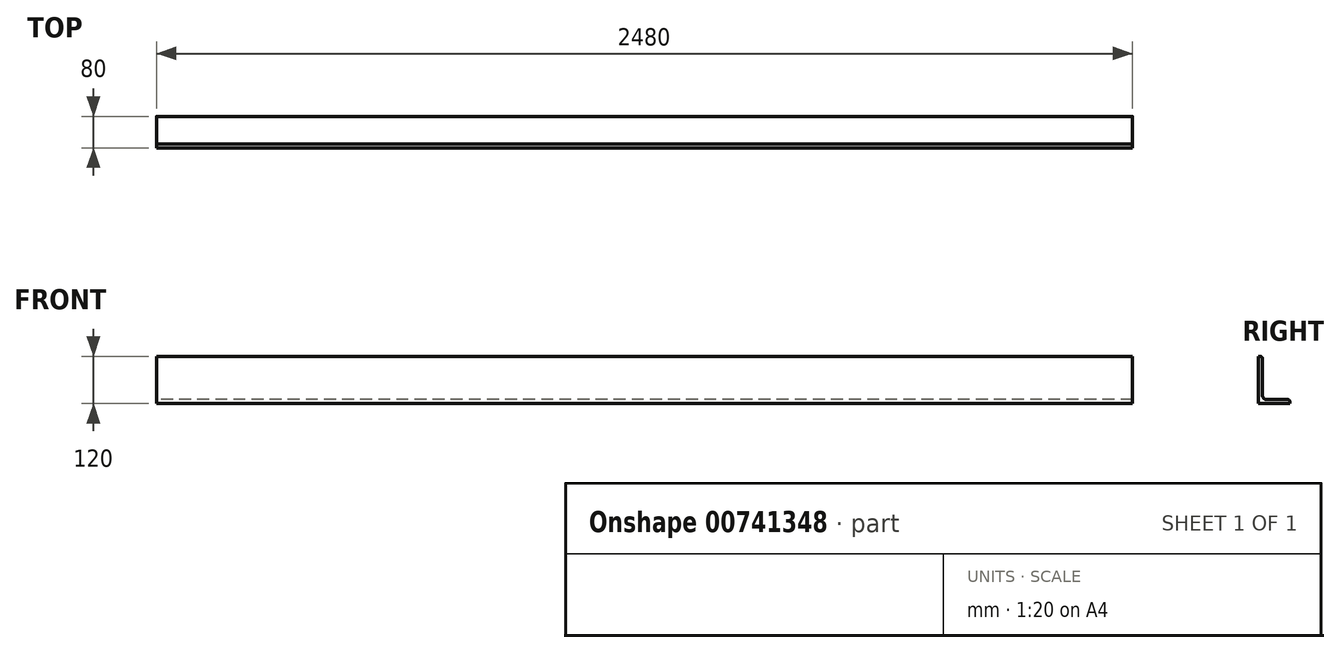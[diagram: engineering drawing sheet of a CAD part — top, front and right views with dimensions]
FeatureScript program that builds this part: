
annotation { "Feature Type Name" : "Feature", "Feature Type Description" : "" }
export const myFeature = defineFeature(function(context is Context, id is Id, definition is map)
    precondition{}
    {
        {
            var Q0;
            Q0=qCreatedBy(makeId("Right.planeOp"),FACE);
            var sketch = newSketch(context, id + "F0", { "sketchPlane" : qUnion([Q0])});
            skLineSegment(sketch, "E0", {"start": v(0, 0) * mm, "end": v(0, 120) * mm});
            skLineSegment(sketch, "E1", {"start": v(0, 0) * mm, "end": v(80, 0) * mm});
            skLineSegment(sketch, "E2", {"start": v(80, 0) * mm, "end": v(80, 4.5) * mm});
            skLineSegment(sketch, "E3", {"start": v(74.5, 10) * mm, "end": v(21, 10) * mm});
            skLineSegment(sketch, "E4", {"start": v(10, 21) * mm, "end": v(10, 114.5) * mm});
            skLineSegment(sketch, "E5", {"start": v(4.5, 120) * mm, "end": v(0, 120) * mm});
            skPoint(sketch, "E6.visualSharp", {"position": v(10, 120) * mm});
            skArc(sketch, "E6.filletArc", {"start": v(10, 114.5) * mm, "mid": v(8.39, 118.39) * mm, "end": v(4.5, 120) * mm});
            skPoint(sketch, "E7.visualSharp", {"position": v(80, 10) * mm});
            skArc(sketch, "E7.filletArc", {"start": v(80, 4.5) * mm, "mid": v(78.39, 8.39) * mm, "end": v(74.5, 10) * mm});
            skPoint(sketch, "E8.visualSharp", {"position": v(10, 10) * mm});
            skArc(sketch, "E8.filletArc", {"start": v(10, 21) * mm, "mid": v(13.22, 13.22) * mm, "end": v(21, 10) * mm});
            skSolve(sketch);
        }
        {
            var Q0;
            Q0=makeQuery(id+"F0.imprint","IMPRINT",FACE,{"disambiguationData":[TD([[makeQuery(id+"F0.imprint","IMPRINT",EDGE,{"derivedFrom":sQuery(id+"F0.wireOp",EDGE,"E0")}),-1.0]])]});
            extrude(context, id + "F1", {"entities" : qUnion([Q0]), "endBound" : BoundingType.SYMMETRIC, "depth" : 2480 * mm, "offsetDistance" : 25 * mm});
        }
    });
